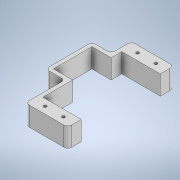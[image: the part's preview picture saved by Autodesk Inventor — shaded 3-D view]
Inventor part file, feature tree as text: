
AUTODESK INVENTOR PART (.ipt)
format: ipt  version: 2020 (Build 240168000, 168)  size: 152,576 bytes
history: native  units: mm
features: sketch x2, extrude x1, hole x1, fillet x1
ambient origin geometry x8: Origin, YZ Plane, XZ Plane, XY Plane, X Axis, Y Axis, Z Axis, Center Point
bodies: Solid1 (feature_tree)
feature tree (5):
  extrude  "Extrusion1"  Depth=2.0mm
  hole  "Hole1"  [1 undecoded]
  fillet  "Fillet1"  Radius=7.0mm
  sketch  "Sketch1"  dims[d1=2.0mm d2=2.0mm]
  sketch  "Sketch2"  dims[d3=2.0mm d4=2.0mm d5=7.0mm d6=7.0mm d7=20.0mm d8=20.0mm d9=41.0mm d10=5.5mm d11=20.0mm d12=10.0mm d13=10.0mm d14=0.0mm d15=4.7mm d16=9.5mm d17=48.0mm d18=3.5mm d19=3.5mm d20=1.5mm d21=6.0mm d22=4.0mm d23=2.0mm d24=90.0deg d25=8.0mm d26=20.594885mm d27=2.0mm]
note: 1 required parameter value undecoded (feature->parameter linkage not recoverable at this tier; creation-order binding heuristic only, values carry confidence <= 0.55)
